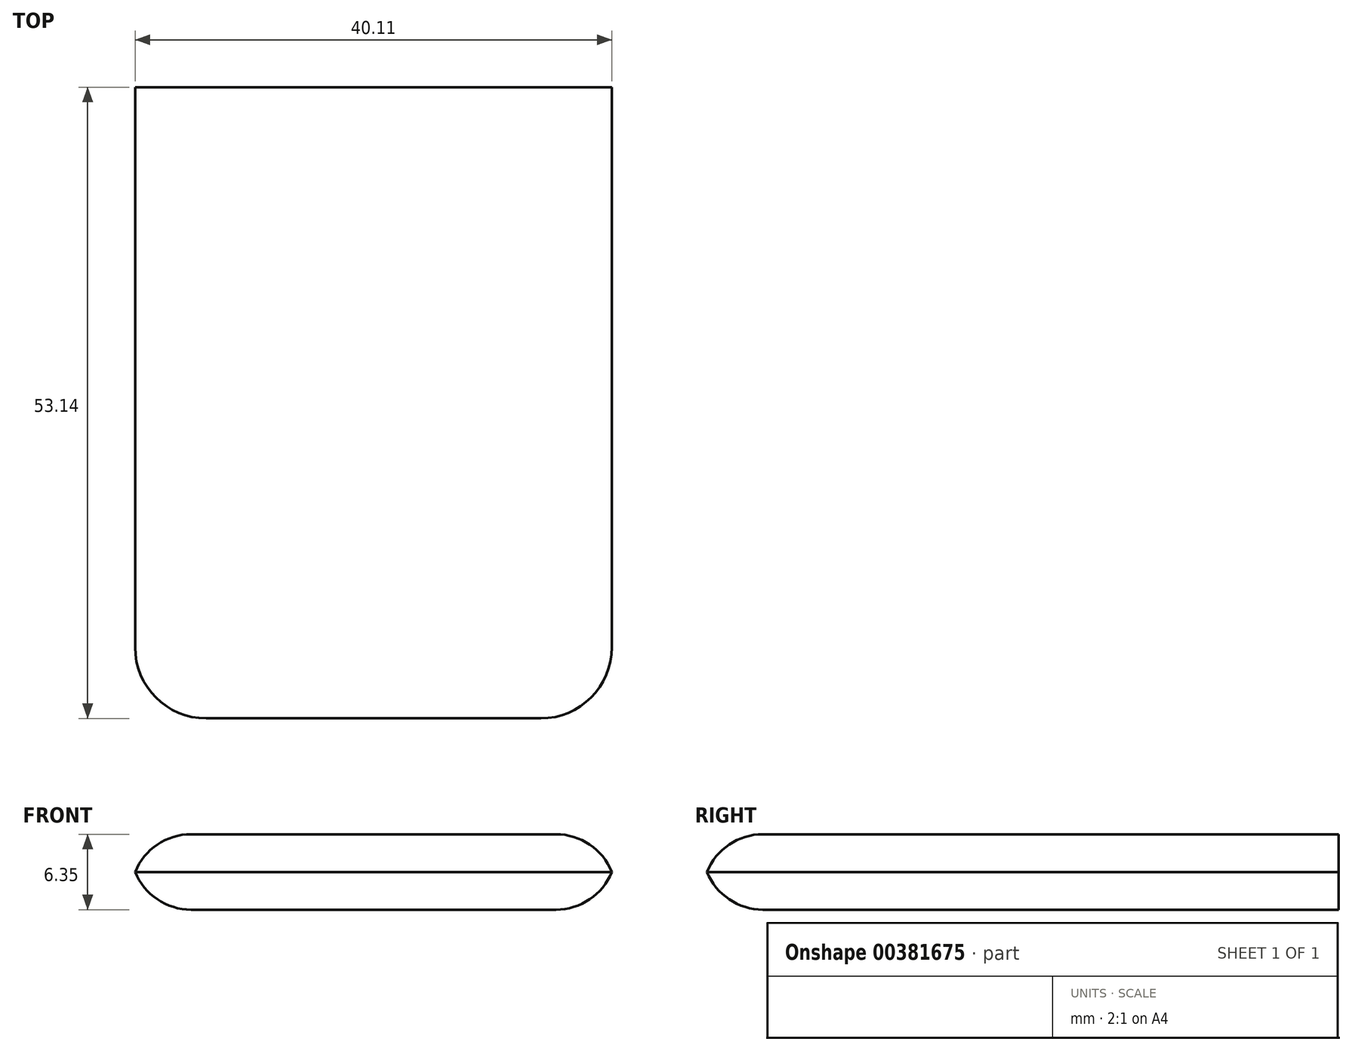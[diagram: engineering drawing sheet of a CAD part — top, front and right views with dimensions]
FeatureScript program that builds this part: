
annotation { "Feature Type Name" : "Feature", "Feature Type Description" : "" }
export const myFeature = defineFeature(function(context is Context, id is Id, definition is map)
    precondition{}
    {
        {
            var Q0;
            Q0=qCreatedBy(makeId("Top.planeOp"),FACE);
            var sketch = newSketch(context, id + "F0", { "sketchPlane" : qUnion([Q0])});
            skLineSegment(sketch, "E0", {"start": v(-20.43, 0) * mm, "end": v(20.42, 0) * mm});
            skLineSegment(sketch, "E1.top", {"start": v(-14.08, -53.5) * mm, "end": v(14.07, -53.5) * mm});
            skLineSegment(sketch, "E1.left", {"start": v(-20.43, 0) * mm, "end": v(-20.43, -47.16) * mm});
            skLineSegment(sketch, "E1.right", {"start": v(20.42, 0) * mm, "end": v(20.42, -47.16) * mm});
            skPoint(sketch, "E2.visualSharp", {"position": v(-20.43, -53.5) * mm});
            skArc(sketch, "E2.filletArc", {"start": v(-20.43, -47.16) * mm, "mid": v(-18.57, -51.65) * mm, "end": v(-14.08, -53.5) * mm});
            skPoint(sketch, "E3.visualSharp", {"position": v(20.42, -53.5) * mm});
            skArc(sketch, "E3.filletArc", {"start": v(14.07, -53.5) * mm, "mid": v(18.56, -51.65) * mm, "end": v(20.42, -47.16) * mm});
            skSolve(sketch);
        }
        {
            var Q0;
            Q0=makeQuery(id+"F0.imprint","IMPRINT",FACE,{"disambiguationData":[TD([[makeQuery(id+"F0.imprint","IMPRINT",EDGE,{"derivedFrom":sQuery(id+"F0.wireOp",EDGE,"E0")}),-1.0]])]});
            extrude(context, id + "F1", {"entities" : qUnion([Q0]), "depth" : 6.35 * mm});
        }
        {
            var Q0;
            Q0=makeQuery(id+"F1.opExtrude","CAP_EDGE",EDGE,{"disambiguationData":[OSD([sQuery(id+"F0.wireOp",EDGE,"E1.right")])],"isStart":false});
            var Q1;
            Q1=makeQuery(id+"F1.opExtrude","CAP_EDGE",EDGE,{"disambiguationData":[OSD([sQuery(id+"F0.wireOp",EDGE,"E3.filletArc")])],"isStart":false});
            var Q2;
            Q2=makeQuery(id+"F1.opExtrude","CAP_EDGE",EDGE,{"disambiguationData":[OSD([sQuery(id+"F0.wireOp",EDGE,"E1.right")])],"isStart":true});
            var Q3;
            Q3=makeQuery(id+"F1.opExtrude","CAP_EDGE",EDGE,{"disambiguationData":[OSD([sQuery(id+"F0.wireOp",EDGE,"E3.filletArc")])],"isStart":true});
            var Q4;
            Q4=makeQuery(id+"F1.opExtrude","CAP_EDGE",EDGE,{"disambiguationData":[OSD([sQuery(id+"F0.wireOp",EDGE,"E1.left")])],"isStart":false});
            var Q5;
            Q5=makeQuery(id+"F1.opExtrude","CAP_EDGE",EDGE,{"disambiguationData":[OSD([sQuery(id+"F0.wireOp",EDGE,"E2.filletArc")])],"isStart":false});
            var Q6;
            Q6=makeQuery(id+"F1.opExtrude","CAP_EDGE",EDGE,{"disambiguationData":[OSD([sQuery(id+"F0.wireOp",EDGE,"E1.top")])],"isStart":true});
            var Q7;
            Q7=makeQuery(id+"F1.opExtrude","CAP_EDGE",EDGE,{"disambiguationData":[OSD([sQuery(id+"F0.wireOp",EDGE,"E1.top")])],"isStart":false});
            var Q8;
            Q8=makeQuery(id+"F1.opExtrude","CAP_EDGE",EDGE,{"disambiguationData":[OSD([sQuery(id+"F0.wireOp",EDGE,"E2.filletArc")])],"isStart":true});
            var Q9;
            Q9=makeQuery(id+"F1.opExtrude","CAP_EDGE",EDGE,{"disambiguationData":[OSD([sQuery(id+"F0.wireOp",EDGE,"E1.left")])],"isStart":true});
            fillet(context, id + "F2", {"entities" : qUnion([Q0, Q1, Q2, Q3, Q4, Q5, Q6, Q7, Q8, Q9]), "radius" : 5.08 * mm, "tangentPropagation" : true, "allowEdgeOverflow" : false});
        }
    });
